# Revit family: Artek_Tables_Kaari Table round_Kaari Table round REB004
name_source: partatom
category: Furniture
revit_build: Autodesk Revit 2017 (Build: 20190508_0315(x64)
units: mm (PartAtom-declared; Revit-internal decimal feet)

## family parameters
Always vertical = Yes
Cut with Voids When Loaded = No
OmniClass Number = 23.40.20.14.17.11
OmniClass Title = Dining Room Tables
Room Calculation Point = No
Shared = No
Work Plane-Based = No

## types (1)
- Kaari Table round REB004
    AssetType = Movable
    BIMObjectName = Artek_Tables_Kaari Table round_Kaari Table round REB004
    Brand = Artek
    Category = Tables
    Collection = Kaari Collection
    Color = Natural/black oak
    ConvergoRefNr = 0190-2009-0031-FI
    Cost = 0 $
    Designer = Ronan & Erwan Bouroullec
    DurationUnit = Years
    IfcExportAs = IfcFurnishingElementType
    IfcExportType = TABLE
    MainColor = Natural/black oak
    Manufacturer = Artek
    ManufacturerName = Artek
    ManufacturerURL = https://www.artek.fi
    Material = Wood/Steel
    Model = Kaari Table round REB004
    ModelNumber = 28305402
    NBSDescription = Tables
    NBSReference = 45-35-86/327
    Name = Kaari Table round REB004
    NominalDepth = 1100 mm
    NominalHeight = 740 mm
    NominalLength = 1100 mm
    Shape = Sculptured
    Size = 1100x740x1100 mm
    URL = https://www.artek.fi
    Uniclass2 = Pr_40_50_21_21
    Uniclass2015Description = Dining tables
    Uniclass2015Reference = Pr_40_50_21_22
    Version = 1
    VersionDate = 11/3/2020
    WarrantyDurationUnit = Years

## geometry (parser evidence)
native form markers: Sweep x5
no freeform markers — native parametric forms only
